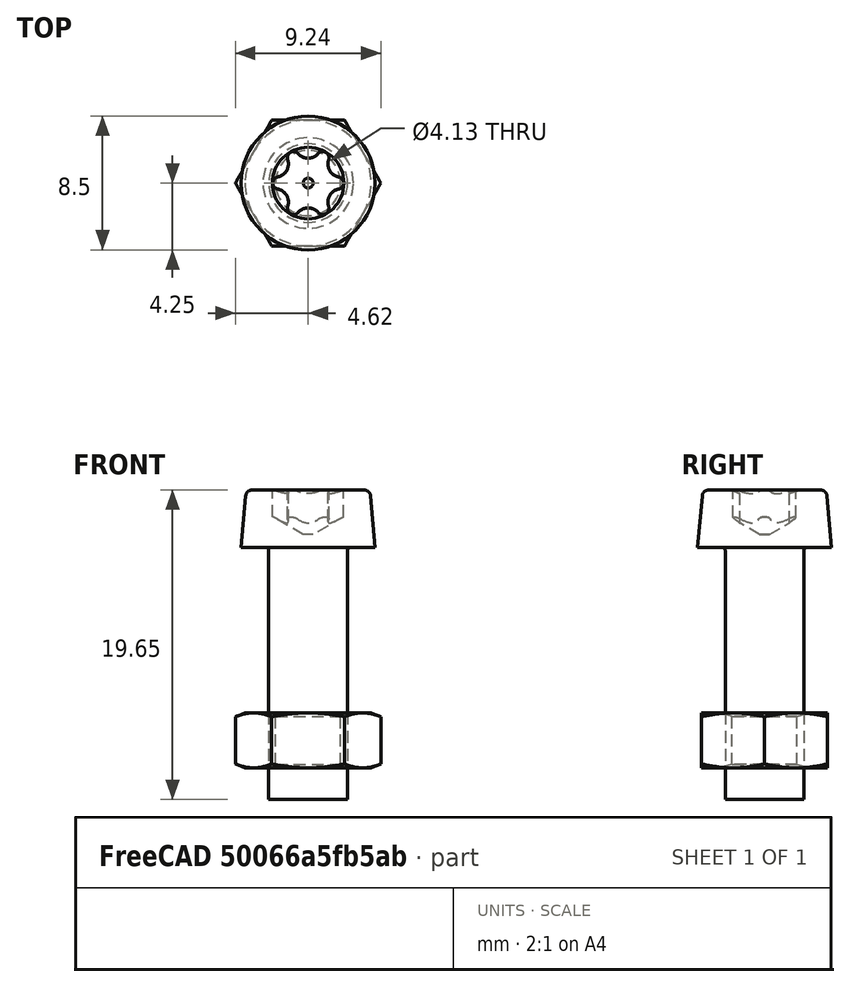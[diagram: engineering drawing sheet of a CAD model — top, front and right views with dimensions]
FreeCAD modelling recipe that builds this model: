
FCSTD DOCUMENT  (FreeCAD 0.21RUnknown)
Label: part16_assembly
License: All rights reserved
LicenseURL: http://en.wikipedia.org/wiki/All_rights_reserved
objects: App::DocumentObjectGroup×3, App::Link×3, Part::FeaturePython×2, PartDesign::CoordinateSystem×1, App::FeaturePython×1, App::Part×1
note: 3 computed .brp shape members not serialized (recipe doc carries the construction recipe); baked Part::Feature solids carry a one-line shape summary decoded from their .brp
EXTERNAL_REF file=part16_clip.FCStd obj=LCS_Origin
EXTERNAL_REF file=part16_clip.FCStd obj=Body
EXTERNAL_REF file=part16_clip.FCStd obj=HoleAxis_1
EXTERNAL_REF file=part16_rectange.FCStd obj=HoleAxis_1
EXTERNAL_REF file=part16_rectange.FCStd obj=Part

FEATURE [App::DocumentObjectGroup] Parts
FEATURE [PartDesign::CoordinateSystem] LCS_Origin
  AttacherType = Attacher::AttachEngine3D
  MapMode = 2
  Support = -> [X_Axis]
FEATURE [App::DocumentObjectGroup] Constraints
FEATURE [App::FeaturePython] Variables  # WARN: FeaturePython — macro-defined, semantics opaque (R4)
  Type = App::PropertyContainer
FEATURE [App::DocumentObjectGroup] Configurations
FEATURE [App::Link] clip
  AttachedBy = #LCS_Origin
  AttachedTo = Parent Assembly#LCS_Origin
  LinkedObject = -> <external part16_clip.FCStd>#Body
  SolverId = Asm4EE
  expr: Placement = LCS_Origin.Placement * AttachmentOffset * part16_clip#LCS_Origin.Placement ^ -1
FEATURE [Part::FeaturePython] Screw  label="M5x16-Screw"  # Fasteners workbench fastener (typed FeaturePython)
  AttachedBy = Origin
  AttachedTo = clip#HoleAxis_1
  Placement = pos=(25,-5,3) rot=(0,0,1;3.14159rad)
  SolverId = Asm4EE
  diameter = 7
  invert = false
  leftHanded = false
  length = 5
  lengthCustom = 16
  matchOuter = false
  offset = 0
  thread = false
  type = 53
  expr: Placement = clip.Placement * part16_clip#HoleAxis_1.Placement * AttachmentOffset
FEATURE [App::Link] rectangle
  AttachedBy = #HoleAxis_1
  AttachedTo = clip#HoleAxis_1
  AttachmentOffset = pos=(0,0,-3) rot=(0,0,1;1.5708rad)
  LinkPlacement = pos=(25,-40,-5) rot=(0,0,1;4.71239rad)
  LinkedObject = -> <external part16_rectange.FCStd>#Part
  Placement = pos=(25,-40,-5) rot=(0,0,1;4.71239rad)
  SolverId = Asm4EE
  expr: Placement = clip.Placement * part16_clip#HoleAxis_1.Placement * AttachmentOffset * part16_rectange#HoleAxis_1.Placement ^ -1
FEATURE [Part::FeaturePython] Nut  label="M5-Nut"  # Fasteners workbench fastener (typed FeaturePython)
  AttachedBy = Origin
  AttachedTo = clip#HoleAxis_1
  AttachmentOffset = pos=(0,0,-14) rot=(0,0,1;0rad)
  Placement = pos=(25,-5,-11) rot=(0,0,1;3.14159rad)
  SolverId = Asm4EE
  diameter = 7
  invert = false
  leftHanded = false
  matchOuter = false
  offset = 0
  thread = false
  type = 31
  expr: Placement = clip.Placement * part16_clip#HoleAxis_1.Placement * AttachmentOffset
FEATURE [App::Link] Body  label="Body_clip#2"
  AttachedBy = #LCS_Origin
  AttachedTo = Parent Assembly#LCS_Origin
  AttachmentOffset = pos=(0,0,-5) rot=(0,1,0;3.14159rad)
  LinkPlacement = pos=(0,0,-5) rot=(0,1,0;3.14159rad)
  LinkedObject = -> <external part16_clip.FCStd>#Body
  Placement = pos=(0,0,-5) rot=(0,1,0;3.14159rad)
  SolverId = Asm4EE
  expr: Placement = LCS_Origin.Placement * AttachmentOffset * part16_clip#LCS_Origin.Placement ^ -1
FEATURE [App::Part] Assembly
  AssemblyType = Part::Link
  Group = -> [LCS_Origin,Constraints,Variables,Configurations,clip,Screw,rectangle,Nut,Body]
  Origin = -> Origin
  Type = Assembly

RESOLVED EXTERNAL PARTS (link-assembly join: the EXTERNAL_REF files above that resolve inside this repo's crawl, each included once):
---- part part16_clip.FCStd = doc fcstd_bde086a9f9f2 ----
FCSTD DOCUMENT  (FreeCAD 0.21RUnknown)
Label: part16_clip
License: All rights reserved
LicenseURL: http://en.wikipedia.org/wiki/All_rights_reserved
objects: Sketcher::SketchObject×2, PartDesign::Pad×1, PartDesign::Pocket×1, PartDesign::CoordinateSystem×1, PartDesign::Line×1, PartDesign::Body×1
note: 9 computed .brp shape members not serialized (recipe doc carries the construction recipe); baked Part::Feature solids carry a one-line shape summary decoded from their .brp

FEATURE [Sketcher::SketchObject] Sketch
  FullyConstrained = true
  MapMode = 5
  Placement = pos=(0,0,0) rot=(1,0,0;1.5708rad)
  Support = -> [XZ_Plane]
  sketch-geometry (10):
    g0: LineSegment StartX=-30 StartY=0 StartZ=0 EndX=-17 EndY=0 EndZ=0
    g1: ArcOfCircle CenterX=0 CenterY=0 CenterZ=0 NormalX=0 NormalY=0 NormalZ=1 AngleXU=0 Radius=20.2237 StartAngle=0.14889 EndAngle=2.9927
    g2: LineSegment StartX=-30 StartY=0 StartZ=0 EndX=-30 EndY=3 EndZ=0
    g3: LineSegment StartX=-30 StartY=3 StartZ=0 EndX=-20 EndY=3 EndZ=0
    g4: LineSegment StartX=30 StartY=0 StartZ=0 EndX=30 EndY=3 EndZ=0
    g5: LineSegment StartX=30 StartY=3 StartZ=0 EndX=20 EndY=3 EndZ=0
    g6: ArcOfCircle CenterX=0 CenterY=0 CenterZ=0 NormalX=0 NormalY=0 NormalZ=1 AngleXU=0 Radius=17.2627 StartAngle=0.174672 EndAngle=2.96692
    g7: LineSegment StartX=-17 StartY=3 StartZ=0 EndX=-17 EndY=0 EndZ=0
    g8: LineSegment StartX=17 StartY=3 StartZ=0 EndX=17 EndY=0 EndZ=0
    g9: LineSegment StartX=17 StartY=0 StartZ=0 EndX=30 EndY=0 EndZ=0
  constraints (30):
    c: PointOnObject(g0,g-1)
    c: PointOnObject(g9,g-1)
    c: Coincident(g2,g3)
    c: Coincident(g3,g1)
    c: Horizontal(g3)
    c: Coincident(g9,g4)
    c: Vertical(g4)
    c: Coincident(g4,g5)
    c: Coincident(g5,g1)
    c: Vertical(g2)
    c: Horizontal(g5)
    c: Equal(g3,g5)
    c: Equal(g2,g4)
    c: Coincident(g2,g0)
    c: DistanceX(g5,g5) = 10
    c: DistanceX(g0,g9) = 60
    c: DistanceY(g0,g2) = 3
    c: Coincident(g1,g-1)
    c: Horizontal(g1,g6)
    c: Horizontal(g6,g6)
    c: Coincident(g7,g6)
    c: Coincident(g8,g6)
    c: Vertical(g8)
    c: DistanceX(g6,g1) = 3
    c: Vertical(g7)
    c: Coincident(g6,g1)
    c: Coincident(g0,g7)
    c: Coincident(g9,g8)
    c: Equal(g9,g0)
    c: PointOnObject(g0,g-1)
FEATURE [PartDesign::Pad] Pad
  Direction = (0,-1,2e-16)
  Length = 10
  Length2 = 10
  Placement = pos=(0,0,0) rot=(1,0,0;1.5708rad)
  Profile = -> Sketch
  ReferenceAxis = -> Sketch [N_Axis]
  Type = 0
FEATURE [Sketcher::SketchObject] Sketch001
  ExternalGeometry = -> [Pad]
  FullyConstrained = true
  MapMode = 5
  Placement = pos=(0,2e-15,3) rot=(0,0,1;3.14159rad)
  Support = -> [Pad]
  sketch-geometry (2):
    g0: Circle CenterX=25 CenterY=5 CenterZ=0 NormalX=0 NormalY=0 NormalZ=1 AngleXU=0 Radius=2.5
    g1: Circle CenterX=-25 CenterY=5 CenterZ=0 NormalX=0 NormalY=0 NormalZ=1 AngleXU=0 Radius=2.5
  constraints (4):
    c: Symmetric(g-5,g-6,g0)
    c: Symmetric(g-4,g-3,g1)
    c: Diameter(g1) = 5
    c: Diameter(g0) = 5
FEATURE [PartDesign::Pocket] Pocket
  BaseFeature = -> Pad
  Direction = (0,-2e-16,-1)
  Length = 3
  Length2 = 5
  Placement = pos=(0,0,0) rot=(1,0,0;1.5708rad)
  Profile = -> Sketch001
  ReferenceAxis = -> Sketch001 [N_Axis]
  Type = 0
FEATURE [PartDesign::CoordinateSystem] LCS_Origin
  AttacherType = Attacher::AttachEngine3D
  Support = -> [Pocket]
FEATURE [PartDesign::Line] HoleAxis_1
  AttacherType = Attacher::AttachEngineLine
  Length = 7.04534
  MapMode = 19
  Placement = pos=(25,-5,3) rot=(0,0,1;3.14159rad)
  ResizeMode = 1
  Support = -> [Pocket]
FEATURE [PartDesign::Body] Body
  Group = -> [Sketch,Pad,Sketch001,Pocket,LCS_Origin,HoleAxis_1]
  Origin = -> Origin
  Tip = -> Pocket
---- part part16_rectange.FCStd = doc fcstd_f95befc6f483 ----
FCSTD DOCUMENT  (FreeCAD 0.21RUnknown)
Label: part16_rectange
License: All rights reserved
LicenseURL: http://en.wikipedia.org/wiki/All_rights_reserved
objects: Sketcher::SketchObject×1, Part::Extrusion×1, PartDesign::Line×1, App::Part×1
note: 3 computed .brp shape members not serialized (recipe doc carries the construction recipe); baked Part::Feature solids carry a one-line shape summary decoded from their .brp

FEATURE [Sketcher::SketchObject] Sketch
  FullyConstrained = true
  sketch-geometry (5):
    g0: LineSegment StartX=-40 StartY=5 StartZ=0 EndX=40 EndY=5 EndZ=0
    g1: LineSegment StartX=40 StartY=5 StartZ=0 EndX=40 EndY=-5 EndZ=0
    g2: LineSegment StartX=40 StartY=-5 StartZ=0 EndX=-40 EndY=-5 EndZ=0
    g3: LineSegment StartX=-40 StartY=-5 StartZ=0 EndX=-40 EndY=5 EndZ=0
    g4: Circle CenterX=-35 CenterY=0 CenterZ=0 NormalX=0 NormalY=0 NormalZ=1 AngleXU=0 Radius=2.5
  constraints (14):
    c: Coincident(g0,g1)
    c: Coincident(g1,g2)
    c: Coincident(g2,g3)
    c: Coincident(g3,g0)
    c: Horizontal(g0)
    c: Horizontal(g2)
    c: Vertical(g1)
    c: Vertical(g3)
    c: Symmetric(g2,g0,g-1)
    c: DistanceX(g0,g0) = 80
    c: DistanceY(g2,g0) = 10
    c: PointOnObject(g4,g-1)
    c: Diameter(g4) = 5
    c: DistanceX(g0,g4) = 5
FEATURE [Part::Extrusion] Extrude
  Base = -> Sketch
  Dir = (0,0,1)
  DirMode = 2
  FaceMakerClass = Part::FaceMakerBullseye
  LengthFwd = 5
  LengthRev = 0
  Solid = true
  Symmetric = false
FEATURE [PartDesign::Line] HoleAxis_1
  AttacherType = Attacher::AttachEngineLine
  Length = 7.04534
  MapMode = 19
  Placement = pos=(-35,0,5) rot=(0,0,1;0rad)
  ResizeMode = 1
  Support = -> [Extrude]
FEATURE [App::Part] Part  label="rectangle"
  Group = -> [Sketch,Extrude,HoleAxis_1]
  Origin = -> Origin
